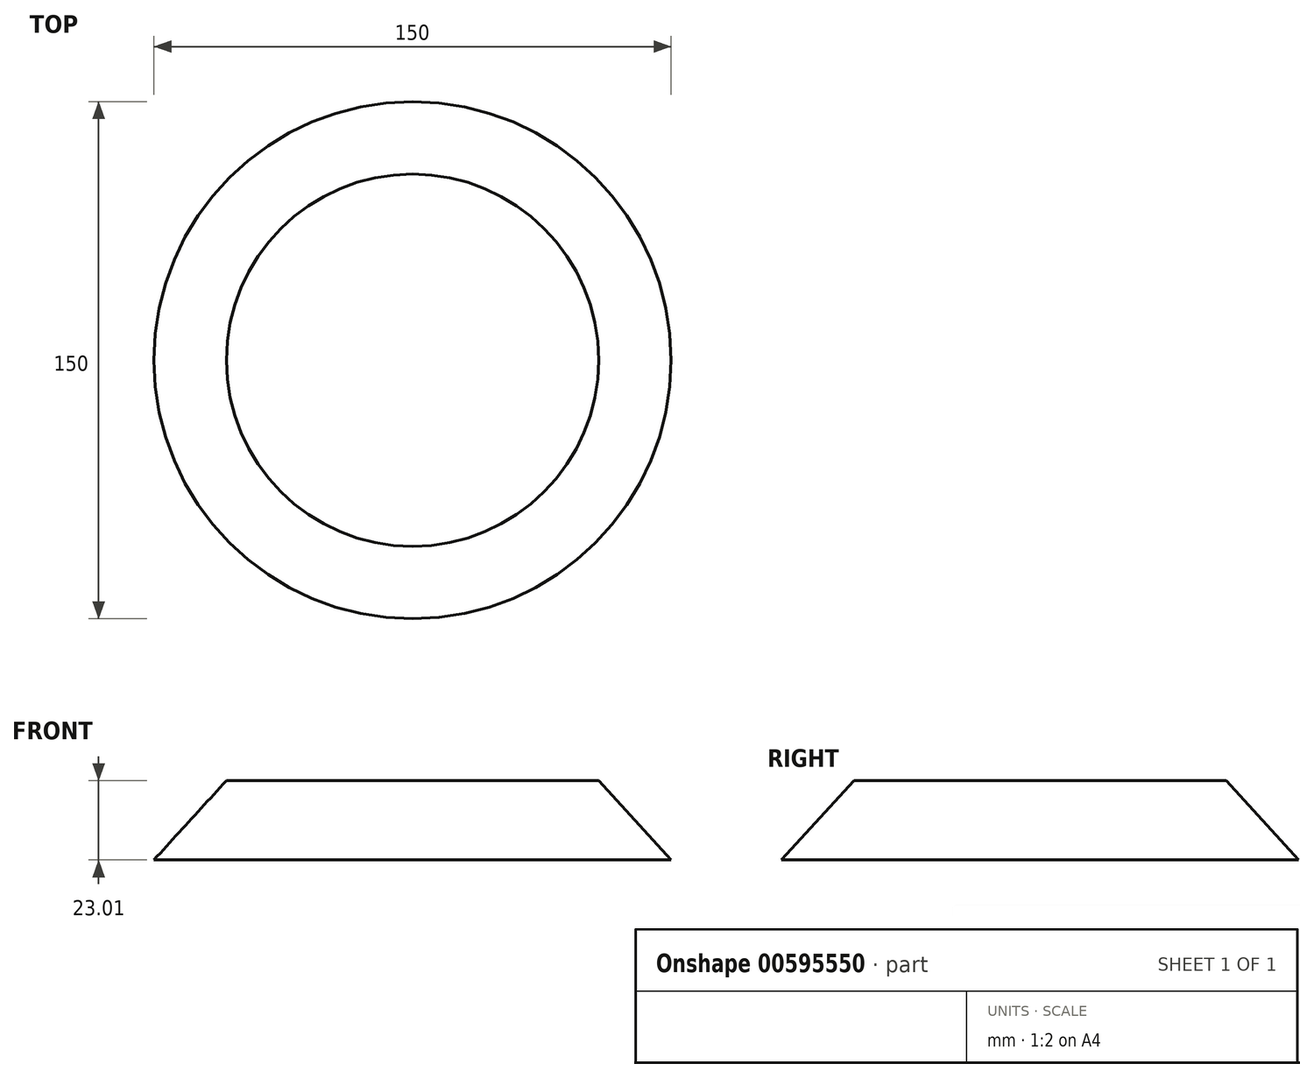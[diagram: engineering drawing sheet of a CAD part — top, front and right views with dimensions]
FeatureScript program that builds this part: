
annotation { "Feature Type Name" : "Feature", "Feature Type Description" : "" }
export const myFeature = defineFeature(function(context is Context, id is Id, definition is map)
    precondition{}
    {
        {
            var Q0;
            Q0=qCreatedBy(makeId("Front.planeOp"),FACE);
            var sketch = newSketch(context, id + "F0", { "sketchPlane" : qUnion([Q0])});
            skLineSegment(sketch, "E0", {"start": v(0, 23.01) * mm, "end": v(-54, 23.01) * mm});
            skLineSegment(sketch, "E1", {"start": v(-54, 23.01) * mm, "end": v(-75, 0) * mm});
            skLineSegment(sketch, "E2", {"start": v(-75, 0) * mm, "end": v(0, 0) * mm});
            skLineSegment(sketch, "E3", {"start": v(0, 0) * mm, "end": v(0, 23.01) * mm});
            skLineSegment(sketch, "E4", {"start": v(-23.64, 23.01) * mm, "end": v(-23.64, 37.4) * mm});
            skLineSegment(sketch, "E5", {"start": v(-23.64, 37.4) * mm, "end": v(-42.64, 37.4) * mm});
            skLineSegment(sketch, "E6", {"start": v(-42.64, 37.4) * mm, "end": v(-42.64, 23.01) * mm});
            skLineSegment(sketch, "E7", {"start": v(-42.64, 23.01) * mm, "end": v(-42.64, 37.4) * mm});
            skLineSegment(sketch, "E8", {"start": v(-42.64, 35.03) * mm, "end": v(-59.29, 41.88) * mm});
            skLineSegment(sketch, "E9", {"start": v(-59.29, 41.88) * mm, "end": v(-61.14, 37.4) * mm});
            skLineSegment(sketch, "E10", {"start": v(-61.14, 37.4) * mm, "end": v(-42.64, 29.78) * mm});
            skLineSegment(sketch, "E11", {"start": v(-42.64, 29.78) * mm, "end": v(-42.64, 35.03) * mm});
            skLineSegment(sketch, "E12", {"start": v(-3.55, 23.01) * mm, "end": v(-3.55, 54.01) * mm});
            skLineSegment(sketch, "E13", {"start": v(-3.55, 54.01) * mm, "end": v(-8.55, 54.01) * mm});
            skLineSegment(sketch, "E14", {"start": v(-8.55, 54.01) * mm, "end": v(-8.55, 23.01) * mm});
            skLineSegment(sketch, "E15", {"start": v(-8.55, 23.01) * mm, "end": v(0, 23.01) * mm});
            skSolve(sketch);
        }
        {
            var Q0;
            {var subQ0=sQuery(id+"F0.wireOp",EDGE,"E1");Q0=makeQuery(id+"F0.imprint","IMPRINT",FACE,{"disambiguationData":[TD([[makeQuery(id+"F0.imprint","IMPRINT",EDGE,{"derivedFrom":subQ0}),1.0]])]});}
            var Q1;
            Q1=sQuery(id+"F0.wireOp",EDGE,"E3");
            revolve(context, id + "F1", {"entities" : qUnion([Q0]), "axis" : qUnion([Q1]), "revolveType" : RevolveType.FULL});
        }
    });
